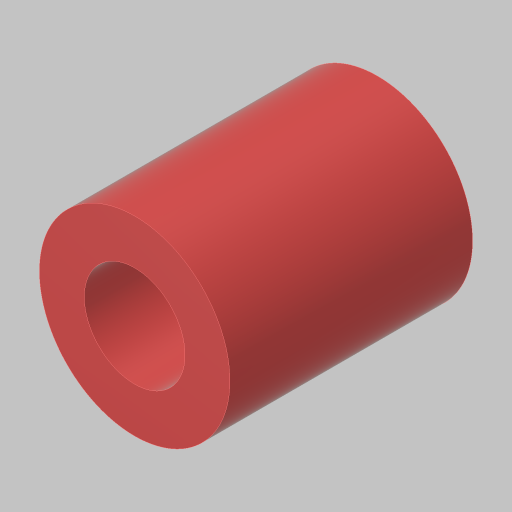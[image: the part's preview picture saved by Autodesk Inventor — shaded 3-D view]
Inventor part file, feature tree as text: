
AUTODESK INVENTOR PART (.ipt)
format: ipt  version: 2023.5 (Build 275446000, 446)  size: 113,664 bytes
history: native  units: in
note: dims shown in document units (in); Inventor stores cm internally (conversion verified against a paired STEP export)
features: extrude x1, sketch x1
ambient origin geometry x8: Origin, YZ Plane, XZ Plane, XY Plane, X Axis, Y Axis, Z Axis, Center Point
bodies: Solid1 (feature_tree)
feature tree (2):
  extrude  "Extrusion1"  Depth=1.35in
  sketch  "Sketch1"  dims[d0=0.56in d1=0.25in d2=1.35in d3=0.0in]
